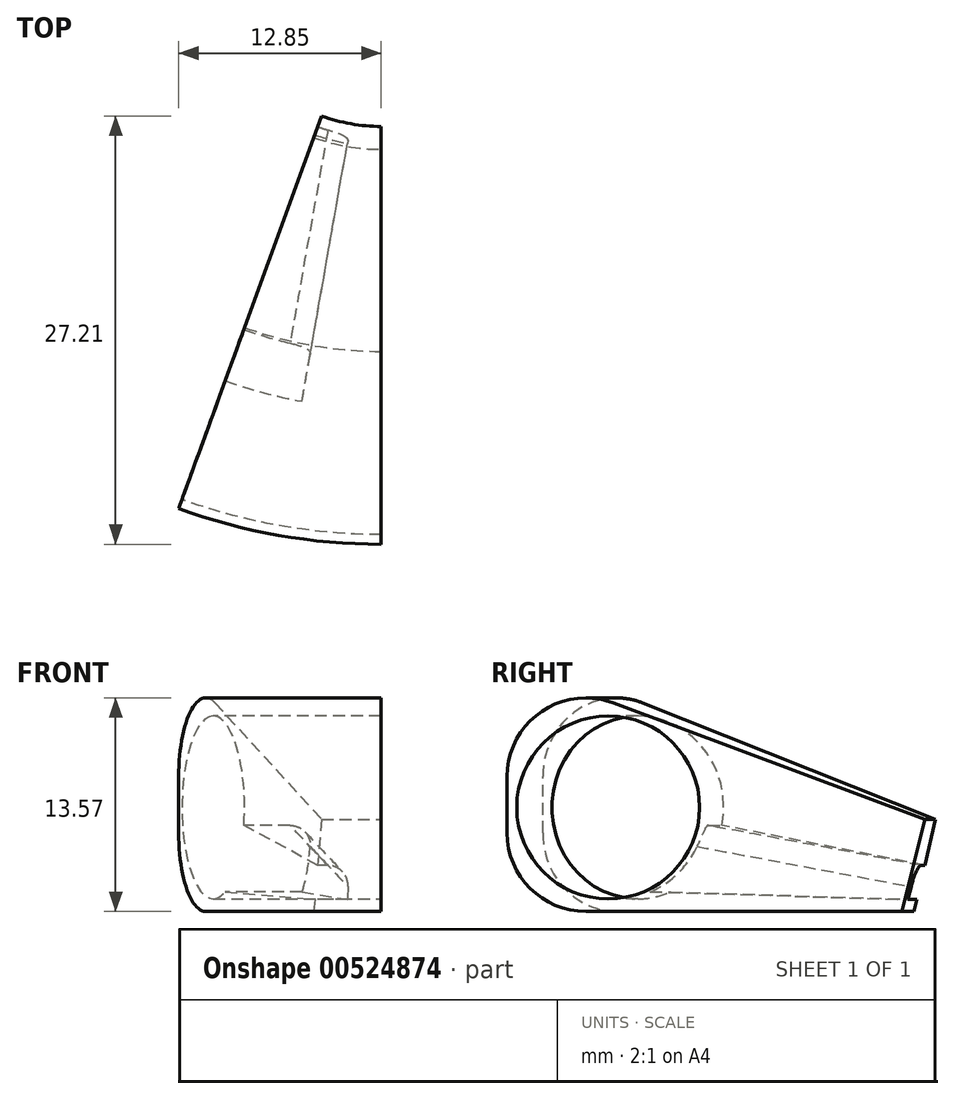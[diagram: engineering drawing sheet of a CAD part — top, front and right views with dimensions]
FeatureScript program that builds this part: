
annotation { "Feature Type Name" : "Feature", "Feature Type Description" : "" }
export const myFeature = defineFeature(function(context is Context, id is Id, definition is map)
    precondition{}
    {
        {
            var Q0;
            Q0=qCreatedBy(makeId("Right.planeOp"),FACE);
            var sketch = newSketch(context, id + "F0", { "sketchPlane" : qUnion([Q0])});
            skCircle(sketch, "E0", {"center": v(0, 0) * mm, "radius": 12.5 * mm, "construction": true});
            skLineSegment(sketch, "E1", {"start": v(-12.5, 0) * mm, "end": v(-32.59, 0) * mm});
            skLineSegment(sketch, "E2", {"start": v(-37.59, 5) * mm, "end": v(-37.59, 8.57) * mm});
            skLineSegment(sketch, "E3", {"start": v(-30.84, 13.25) * mm, "end": v(-11.04, 5.86) * mm});
            skLineSegment(sketch, "E4", {"start": v(-11.04, 5.86) * mm, "end": v(-12.5, 0) * mm});
            skPoint(sketch, "E5.visualSharp", {"position": v(-37.59, 15.77) * mm});
            skArc(sketch, "E5.filletArc", {"start": v(-30.84, 13.25) * mm, "mid": v(-35.44, 12.67) * mm, "end": v(-37.59, 8.57) * mm});
            skPoint(sketch, "E6.visualSharp", {"position": v(-37.59, 0) * mm});
            skArc(sketch, "E6.filletArc", {"start": v(-37.59, 5) * mm, "mid": v(-36.12, 1.46) * mm, "end": v(-32.59, 0) * mm});
            skCircle(sketch, "E7", {"center": v(-31.17, 6.61) * mm, "radius": 5.8 * mm});
            skSolve(sketch);
        }
        {
            var Q0;
            Q0=qCreatedBy(makeId("Front.planeOp"),FACE);
            var sketch = newSketch(context, id + "F1", { "sketchPlane" : qUnion([Q0])});
            skLineSegment(sketch, "E8", {"start": v(0, 63.85) * mm, "end": v(0, -55.6) * mm});
            skSolve(sketch);
        }
        {
            var Q0;
            Q0=makeQuery(id+"F0.imprint","IMPRINT",FACE,{"disambiguationData":[TD([[makeQuery(id+"F0.imprint","IMPRINT",EDGE,{"derivedFrom":sQuery(id+"F0.wireOp",EDGE,"E1")}),-1.0]])]});
            var Q1;
            Q1=sQuery(id+"F1.wireOp",EDGE,"E8");
            revolve(context, id + "F2", {"entities" : qUnion([Q0]), "axis" : qUnion([Q1]), "revolveType" : RevolveType.ONE_DIRECTION, "angle" : 20 * degree});
        }
        {
            var Q0;
            Q0=makeQuery(id+"F2.opRevolve","CAP_FACE",FACE,{"disambiguationData":[OSD([sQuery(id+"F0.wireOp",EDGE,"E1"),sQuery(id+"F0.wireOp",EDGE,"E2"),sQuery(id+"F0.wireOp",EDGE,"E3"),sQuery(id+"F0.wireOp",EDGE,"E4"),sQuery(id+"F0.wireOp",EDGE,"E5.filletArc"),sQuery(id+"F0.wireOp",EDGE,"E6.filletArc"),sQuery(id+"F0.wireOp",EDGE,"E7")])],"isStart":false});
            var sketch = newSketch(context, id + "F3", { "sketchPlane" : qUnion([Q0])});
            skLineSegment(sketch, "E9", {"start": v(28.94, 1.25) * mm, "end": v(12.31, 0.76) * mm});
            skLineSegment(sketch, "E10", {"start": v(12.31, 0.76) * mm, "end": v(11.77, 2.93) * mm});
            skLineSegment(sketch, "E11", {"start": v(11.77, 2.93) * mm, "end": v(25.47, 5.47) * mm});
            skCircle(sketch, "E12.0", {"center": v(31.17, 6.61) * mm, "radius": 5.8 * mm});
            skSolve(sketch);
        }
        {
            var Q0;
            {var subQ0=sQuery(id+"F3.wireOp",EDGE,"E9");Q0=makeQuery(id+"F3.imprint","IMPRINT",FACE,{"disambiguationData":[TD([[makeQuery(id+"F3.imprint","IMPRINT",EDGE,{"derivedFrom":subQ0}),-1.0]])]});}
            var Q1;
            Q1=sQuery(id+"F1.wireOp",EDGE,"E8");
            revolve(context, id + "F4", {"operationType" : NewBodyOperationType.REMOVE, "entities" : qUnion([Q0]), "axis" : qUnion([Q1]), "revolveType" : RevolveType.ONE_DIRECTION, "oppositeDirection" : true, "angle" : 10 * degree});
        }
        {
            var Q0;
            Q0=makeQuery(id+"F4.boolean.opBoolean","COPY",EDGE,{"derivedFrom":makeQuery(id+"F4.opRevolve","CAP_EDGE",EDGE,{"disambiguationData":[OSD([sQuery(id+"F3.wireOp",EDGE,"E11")])],"isStart":false})});
            fillet(context, id + "F5", {"entities" : qUnion([Q0]), "radius" : 1.4 * mm, "tangentPropagation" : true, "allowEdgeOverflow" : false});
        }
    });
